# Revit family: CF458 (6RED+2RJ45)
name_source: partatom
category: Aparatos eléctricos
revit_build: Autodesk Revit 2016 (Build: 20150220_1215(x64)
units: mm (PartAtom-declared; Revit-internal decimal feet)

## family parameters
Anfitrión = Cara
Compartido = No
Corte con vacíos al cargar = No
Cota de conector redondo = Diámetro de uso
Mantener orientación de anotación = No
Número OmniClass = 23.80.50.11.11
Punto de cálculo de habitación = No
Tipo de pieza = Normal
Título OmniClass = Receptacle Terminal Units

## types (1)
- Gama 45
    Acabado caja = Blanco nieve RAL9010
    Acabado marco = Gris RAL7011
    CF458 (AltoxLargoxAncho) = 69,50x254x254 mm
    Capacidad = 4 módulos 45
    Carga eléctrica = Potencia
    Compatibilidad = Gama 45
    Composición = Cubeta, Marcos (4ud), Anclajes (4ud), Pasacables (2ud), Tapa metálica
    Código de montaje = D5020100
    Descripción = Caja de conexiones empotrable CF45
    Elevación por defecto = 1200 mm
    Fabricante = MMCONECTA
    Factor de potencia = 1
    Instalación = Empotrado en suelo técnico
    Materia prima = Policarbonato libre de halógenos
    Modelo = CF458
    Normativas = UNE 60670 / Marcado CE
    Polos = 1
    Potencia aparente = 3500 W
    URL = http://www.mmconecta.com
    Voltaje = 230 V
    Ø tubos G = 25 mm  [stored 0.082021 ft]

note: [stored X ft] marks values corroborated as IEEE doubles in the binary element streams (Revit-internal decimal feet)

## geometry (parser evidence)
native form markers: Blend x4
no freeform markers — native parametric forms only
